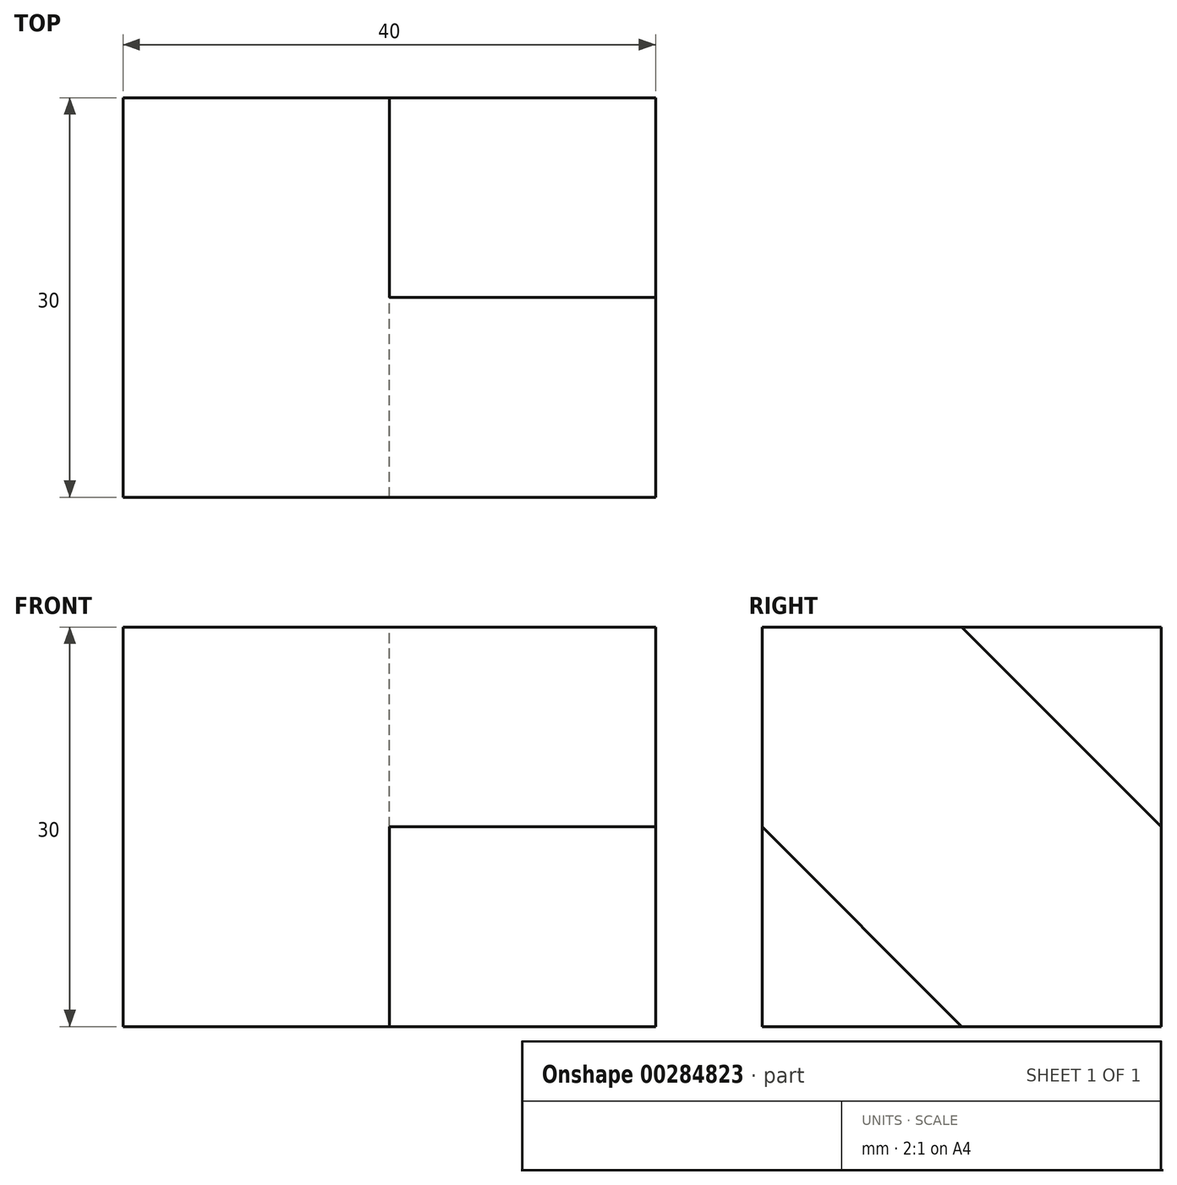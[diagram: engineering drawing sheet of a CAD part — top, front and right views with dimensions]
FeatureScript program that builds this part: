
annotation { "Feature Type Name" : "Feature", "Feature Type Description" : "" }
export const myFeature = defineFeature(function(context is Context, id is Id, definition is map)
    precondition{}
    {
        {
            var Q0;
            Q0=qCreatedBy(makeId("Right.planeOp"),FACE);
            var sketch = newSketch(context, id + "F0", { "sketchPlane" : qUnion([Q0])});
            skLineSegment(sketch, "E0.bottom", {"start": v(0, 0) * mm, "end": v(30, 0) * mm});
            skLineSegment(sketch, "E0.top", {"start": v(0, 30) * mm, "end": v(30, 30) * mm});
            skLineSegment(sketch, "E0.left", {"start": v(0, 0) * mm, "end": v(0, 30) * mm});
            skLineSegment(sketch, "E0.right", {"start": v(30, 0) * mm, "end": v(30, 30) * mm});
            skLineSegment(sketch, "E1", {"start": v(0, 15) * mm, "end": v(30, 15) * mm});
            skLineSegment(sketch, "E2", {"start": v(15, 30) * mm, "end": v(15, 0) * mm});
            skSolve(sketch);
        }
        {
            var Q0;
            Q0=qSketchRegion(id+"F0",true);
            extrude(context, id + "F1", {"entities" : qUnion([Q0]), "depth" : 20 * mm});
        }
        {
            var Q0;
            {var subQ0=sQuery(id+"F0.wireOp",EDGE,"E0.right");var subQ1=sQuery(id+"F0.wireOp",EDGE,"E0.bottom");var subQ2=makeQuery(id+"F0.imprint","INTERSECT",VERTEX,{"derivedFrom":[subQ1,subQ0]});Q0=makeQuery(id+"F0.imprint","IMPRINT",FACE,{"disambiguationData":[TD([[makeQuery(id+"F0.imprint","IMPRINT",EDGE,{"disambiguationData":[TD([[subQ2,1.0]])],"derivedFrom":subQ1}),1.0]])]});}
            var Q1;
            {var subQ0=sQuery(id+"F0.wireOp",EDGE,"E0.right");var subQ1=sQuery(id+"F0.wireOp",EDGE,"E0.top");var subQ2=makeQuery(id+"F0.imprint","INTERSECT",VERTEX,{"derivedFrom":[subQ1,subQ0]});Q1=makeQuery(id+"F0.imprint","IMPRINT",FACE,{"disambiguationData":[TD([[makeQuery(id+"F0.imprint","IMPRINT",EDGE,{"disambiguationData":[TD([[subQ2,1.0]])],"derivedFrom":subQ1}),-1.0]])]});}
            var Q2;
            {var subQ0=sQuery(id+"F0.wireOp",EDGE,"E0.left");var subQ1=sQuery(id+"F0.wireOp",EDGE,"E0.top");var subQ2=makeQuery(id+"F0.imprint","INTERSECT",VERTEX,{"derivedFrom":[subQ1,subQ0]});Q2=makeQuery(id+"F0.imprint","IMPRINT",FACE,{"disambiguationData":[TD([[makeQuery(id+"F0.imprint","IMPRINT",EDGE,{"disambiguationData":[TD([[subQ2,-1.0]])],"derivedFrom":subQ1}),-1.0]])]});}
            extrude(context, id + "F2", {"entities" : qUnion([Q0, Q1, Q2]), "operationType" : NewBodyOperationType.ADD, "depth" : 40 * mm});
        }
        {
            var Q0;
            Q0=makeQuery(id+"F2.opExtrude","CAP_FACE",FACE,{"disambiguationData":[OSD([sQuery(id+"F0.wireOp",EDGE,"E0.bottom"),sQuery(id+"F0.wireOp",EDGE,"E0.top"),sQuery(id+"F0.wireOp",EDGE,"E0.left"),sQuery(id+"F0.wireOp",EDGE,"E0.right"),sQuery(id+"F0.wireOp",EDGE,"E1"),sQuery(id+"F0.wireOp",EDGE,"E2")])],"isStart":false});
            var sketch = newSketch(context, id + "F3", { "sketchPlane" : qUnion([Q0])});
            skLineSegment(sketch, "E3", {"start": v(15, 30) * mm, "end": v(30, 15) * mm});
            skSolve(sketch);
        }
        {
            var Q0;
            {var subQ0=sQuery(id+"F3.wireOp",EDGE,"E3");Q0=makeQuery(id+"F3.imprint","IMPRINT",FACE,{"disambiguationData":[TD([[makeQuery(id+"F3.imprint","IMPRINT",EDGE,{"derivedFrom":subQ0}),1.0]])]});}
            extrude(context, id + "F4", {"entities" : qUnion([Q0]), "operationType" : NewBodyOperationType.REMOVE, "oppositeDirection" : true, "depth" : 20 * mm});
        }
        {
            var Q0;
            Q0=makeQuery(id+"F1.opExtrude","CAP_FACE",FACE,{"disambiguationData":[OSD([sQuery(id+"F0.wireOp",EDGE,"E0.bottom"),sQuery(id+"F0.wireOp",EDGE,"E0.top"),sQuery(id+"F0.wireOp",EDGE,"E0.left"),sQuery(id+"F0.wireOp",EDGE,"E0.right")])],"isStart":false});
            var sketch = newSketch(context, id + "F5", { "sketchPlane" : qUnion([Q0])});
            skLineSegment(sketch, "E4", {"start": v(0, 15) * mm, "end": v(15, 0) * mm});
            skSolve(sketch);
        }
        {
            var Q0;
            Q0=makeQuery(id+"F5.imprint","IMPRINT",FACE,{"disambiguationData":[TD([[makeQuery(id+"F5.imprint","IMPRINT",EDGE,{"derivedFrom":sQuery(id+"F5.wireOp",EDGE,"E4")}),1.0]])]});
            extrude(context, id + "F6", {"entities" : qUnion([Q0]), "operationType" : NewBodyOperationType.ADD, "depth" : 20 * mm});
        }
    });
